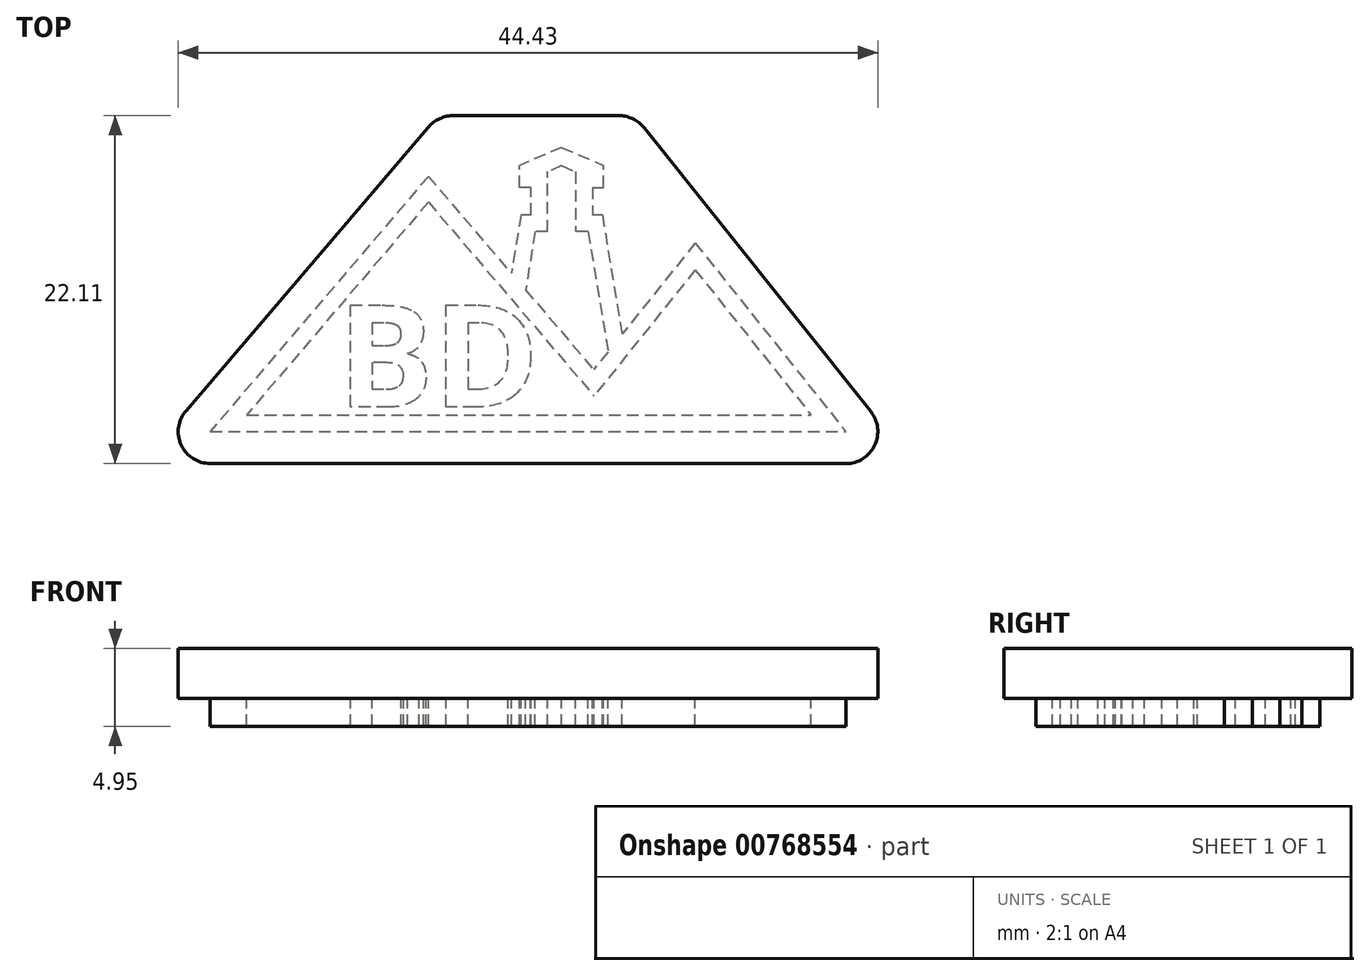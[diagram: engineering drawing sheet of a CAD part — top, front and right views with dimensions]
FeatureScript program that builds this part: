
annotation { "Feature Type Name" : "Feature", "Feature Type Description" : "" }
export const myFeature = defineFeature(function(context is Context, id is Id, definition is map)
    precondition{}
    {
        {
            var Q0;
            Q0=qCreatedBy(makeId("Top.planeOp"),FACE);
            var sketch = newSketch(context, id + "F0", { "sketchPlane" : qUnion([Q0])});
            skPoint(sketch, "E0.middle", {"position": v(0, 0) * mm});
            skLineSegment(sketch, "E1.1", {"start": v(-10.6, 2.98) * mm, "end": v(-5.95, -2.81) * mm});
            skLineSegment(sketch, "E1.2", {"start": v(6.35, 7.21) * mm, "end": v(1.09, 1.05) * mm});
            skLineSegment(sketch, "E2.0", {"start": v(-10.6, 1.27) * mm, "end": v(-17.94, -7.93) * mm});
            skLineSegment(sketch, "E3.0", {"start": v(6.35, 5.57) * mm, "end": v(17.9, -7.93) * mm});
            skLineSegment(sketch, "E3.1", {"start": v(6.35, 5.57) * mm, "end": v(-4.17, -6.74) * mm});
            skLineSegment(sketch, "E3.2", {"start": v(-10.6, 1.27) * mm, "end": v(-4.17, -6.74) * mm});
            skLineSegment(sketch, "E4.0", {"start": v(17.9, -7.93) * mm, "end": v(-17.94, -7.93) * mm});
            skPoint(sketch, "E5", {"position": v(-17.94, -7.93) * mm});
            skPoint(sketch, "E6", {"position": v(17.9, -7.93) * mm});
            skPoint(sketch, "E7", {"position": v(-4.15, -5.07) * mm});
            skPoint(sketch, "E8", {"position": v(-4.17, -6.74) * mm});
            skPoint(sketch, "E9", {"position": v(6.35, 5.57) * mm});
            skPoint(sketch, "E10", {"position": v(-10.6, 1.27) * mm});
            skPoint(sketch, "E11", {"position": v(6.35, 7.21) * mm});
            skPoint(sketch, "E12", {"position": v(-10.6, 2.98) * mm});
            skLineSegment(sketch, "E13.0", {"start": v(-4.7, 4.76) * mm, "end": v(-5.95, -2.81) * mm});
            skLineSegment(sketch, "E13.1", {"start": v(-4.7, 4.76) * mm, "end": v(-4.06, 4.76) * mm});
            skLineSegment(sketch, "E13.2", {"start": v(-0.15, 6.5) * mm, "end": v(0.56, 6.5) * mm});
            skLineSegment(sketch, "E13.3", {"start": v(-0.15, 4.76) * mm, "end": v(-0.15, 6.5) * mm});
            skLineSegment(sketch, "E13.4", {"start": v(-0.15, 4.76) * mm, "end": v(0.48, 4.76) * mm});
            skLineSegment(sketch, "E13.5", {"start": v(0.48, 4.76) * mm, "end": v(1.09, 1.05) * mm});
            skLineSegment(sketch, "E13.6", {"start": v(0.56, 6.5) * mm, "end": v(0.56, 7.9) * mm});
            skLineSegment(sketch, "E13.7", {"start": v(-2.1, 9.05) * mm, "end": v(0.56, 7.9) * mm});
            skLineSegment(sketch, "E13.8", {"start": v(-2.1, 9.05) * mm, "end": v(-4.78, 7.9) * mm});
            skLineSegment(sketch, "E13.9", {"start": v(-4.78, 6.5) * mm, "end": v(-4.78, 7.9) * mm});
            skLineSegment(sketch, "E13.10", {"start": v(-4.06, 6.5) * mm, "end": v(-4.78, 6.5) * mm});
            skLineSegment(sketch, "E13.11", {"start": v(-4.06, 6.5) * mm, "end": v(-4.06, 4.76) * mm});
            skLineSegment(sketch, "E14.0", {"start": v(-3.79, 3.7) * mm, "end": v(-5.06, -3.93) * mm});
            skLineSegment(sketch, "E14.1", {"start": v(-3.79, 3.7) * mm, "end": v(-3, 3.7) * mm});
            skLineSegment(sketch, "E14.2", {"start": v(-3, 7.5) * mm, "end": v(-3, 3.7) * mm});
            skLineSegment(sketch, "E14.3", {"start": v(-2.1, 7.89) * mm, "end": v(-3, 7.5) * mm});
            skLineSegment(sketch, "E14.4", {"start": v(-0.43, 3.7) * mm, "end": v(0.18, 0) * mm});
            skLineSegment(sketch, "E14.5", {"start": v(-1.22, 3.7) * mm, "end": v(-0.43, 3.7) * mm});
            skLineSegment(sketch, "E14.6", {"start": v(-1.22, 3.7) * mm, "end": v(-1.22, 7.5) * mm});
            skLineSegment(sketch, "E14.7", {"start": v(-2.1, 7.89) * mm, "end": v(-1.22, 7.5) * mm});
            skPoint(sketch, "E15", {"position": v(-5.95, -2.81) * mm});
            skPoint(sketch, "E16", {"position": v(-5.06, -3.93) * mm});
            skPoint(sketch, "E17", {"position": v(0.18, 0) * mm});
            skPoint(sketch, "E18", {"position": v(1.09, 1.05) * mm});
            skPoint(sketch, "E19", {"position": v(20.2, -9) * mm});
            skPoint(sketch, "E20", {"position": v(-20.16, -9) * mm});
            skLineSegment(sketch, "E21.trimOffspring", {"start": v(0.18, 0) * mm, "end": v(-4.15, -5.07) * mm});
            skLineSegment(sketch, "E22.trimOffspring", {"start": v(-5.06, -3.93) * mm, "end": v(-4.15, -5.07) * mm});
            skLineSegment(sketch, "E23", {"start": v(20.2, -9) * mm, "end": v(-20.16, -9) * mm});
            skLineSegment(sketch, "E24", {"start": v(6.35, 7.21) * mm, "end": v(20.2, -9) * mm});
            skLineSegment(sketch, "E25", {"start": v(-10.6, 2.98) * mm, "end": v(-20.16, -9) * mm});
            skText(sketch, "E26", { "text": "BD", "fontName": "NotoSans-Bold.ttf"});
            skLineSegment(sketch, "E27", {"start": v(-20.16, -11.03) * mm, "end": v(20.2, -11.03) * mm});
            skArc(sketch, "E28", {"start": v(-21.75, -7.73) * mm, "mid": v(-21.99, -9.88) * mm, "end": v(-20.16, -11.03) * mm});
            skArc(sketch, "E29", {"start": v(20.2, -11.03) * mm, "mid": v(22.05, -9.85) * mm, "end": v(21.75, -7.68) * mm});
            skLineSegment(sketch, "E30", {"start": v(-5.69, 11.08) * mm, "end": v(4.72, 11.08) * mm});
            skArc(sketch, "E31", {"start": v(6.36, 10.32) * mm, "mid": v(5.63, 10.88) * mm, "end": v(4.72, 11.08) * mm});
            skArc(sketch, "E32", {"start": v(-5.69, 11.08) * mm, "mid": v(-6.62, 10.87) * mm, "end": v(-7.37, 10.27) * mm});
            skLineSegment(sketch, "E33.trimOffspring", {"start": v(-7.37, 10.27) * mm, "end": v(-21.75, -7.73) * mm});
            skLineSegment(sketch, "E34.trimOffspring", {"start": v(6.36, 10.32) * mm, "end": v(21.75, -7.68) * mm});
            skPoint(sketch, "E35.start.orphan", {"position": v(0, 19.5) * mm});
            skLineSegment(sketch, "E36", {"start": v(24.3, 18.38) * mm, "end": v(24.3, -20.56) * mm});
            skLineSegment(sketch, "E37.MirrorCS", {"start": v(52.66, 6.5) * mm, "end": v(53.37, 6.5) * mm});
            skLineSegment(sketch, "E38.MirrorCS", {"start": v(50.7, 7.89) * mm, "end": v(51.6, 7.5) * mm});
            skLineSegment(sketch, "E39.MirrorCS", {"start": v(50.7, 7.89) * mm, "end": v(49.82, 7.5) * mm});
            skLineSegment(sketch, "E40.MirrorCS", {"start": v(48.75, 4.76) * mm, "end": v(48.12, 4.76) * mm});
            skLineSegment(sketch, "E41.MirrorCS", {"start": v(49.03, 3.7) * mm, "end": v(48.42, 0) * mm});
            skLineSegment(sketch, "E42.MirrorCS", {"start": v(52.66, 6.5) * mm, "end": v(52.66, 4.76) * mm});
            skLineSegment(sketch, "E43.MirrorCS", {"start": v(53.65, -3.93) * mm, "end": v(52.75, -5.07) * mm});
            skLineSegment(sketch, "E44.MirrorCS", {"start": v(49.82, 3.7) * mm, "end": v(49.03, 3.7) * mm});
            skLineSegment(sketch, "E45.MirrorCS", {"start": v(53.37, 6.5) * mm, "end": v(53.37, 7.9) * mm});
            skLineSegment(sketch, "E46.MirrorCS", {"start": v(49.82, 3.7) * mm, "end": v(49.82, 7.5) * mm});
            skLineSegment(sketch, "E47.MirrorCS", {"start": v(48.12, 4.76) * mm, "end": v(47.51, 1.05) * mm});
            skLineSegment(sketch, "E48.MirrorCS", {"start": v(48.75, 4.76) * mm, "end": v(48.75, 6.5) * mm});
            skLineSegment(sketch, "E49.MirrorCS", {"start": v(48.75, 6.5) * mm, "end": v(48.04, 6.5) * mm});
            skLineSegment(sketch, "E50.MirrorCS", {"start": v(53.3, 4.76) * mm, "end": v(52.66, 4.76) * mm});
            skLineSegment(sketch, "E51.MirrorCS", {"start": v(52.39, 3.7) * mm, "end": v(51.6, 3.7) * mm});
            skLineSegment(sketch, "E52.MirrorCS", {"start": v(51.6, 7.5) * mm, "end": v(51.6, 3.7) * mm});
            skArc(sketch, "E53.MirrorCS", {"start": v(54.28, 11.08) * mm, "mid": v(55.22, 10.87) * mm, "end": v(55.97, 10.27) * mm});
            skLineSegment(sketch, "E54.MirrorCS", {"start": v(50.7, 9.05) * mm, "end": v(48.04, 7.9) * mm});
            skLineSegment(sketch, "E55.MirrorCS", {"start": v(48.04, 6.5) * mm, "end": v(48.04, 7.9) * mm});
            skLineSegment(sketch, "E56.MirrorCS", {"start": v(50.7, 9.05) * mm, "end": v(53.37, 7.9) * mm});
            skArc(sketch, "E57.MirrorCS", {"start": v(42.23, 10.32) * mm, "mid": v(42.97, 10.88) * mm, "end": v(43.87, 11.08) * mm});
            skLineSegment(sketch, "E58.MirrorCS", {"start": v(59.19, 1.27) * mm, "end": v(66.54, -7.93) * mm});
            skArc(sketch, "E59.MirrorCS", {"start": v(70.34, -7.73) * mm, "mid": v(70.59, -9.88) * mm, "end": v(68.76, -11.03) * mm});
            skPoint(sketch, "E60.MirrorP", {"position": v(48.6, 0) * mm});
            skArc(sketch, "E61.MirrorCS", {"start": v(28.4, -11.03) * mm, "mid": v(26.55, -9.85) * mm, "end": v(26.85, -7.68) * mm});
            skLineSegment(sketch, "E62.MirrorCS", {"start": v(42.25, 7.21) * mm, "end": v(28.4, -9) * mm});
            skLineSegment(sketch, "E63.MirrorCS", {"start": v(48.42, 0) * mm, "end": v(52.75, -5.07) * mm});
            skLineSegment(sketch, "E64.MirrorCS", {"start": v(30.7, -7.93) * mm, "end": v(66.54, -7.93) * mm});
            skPoint(sketch, "E65.MirrorP", {"position": v(52.77, -6.74) * mm});
            skPoint(sketch, "E66.MirrorP", {"position": v(59.19, 1.27) * mm});
            skPoint(sketch, "E67.MirrorP", {"position": v(42.25, 5.57) * mm});
            skPoint(sketch, "E68.MirrorP", {"position": v(52.75, -5.07) * mm});
            skPoint(sketch, "E69.MirrorP", {"position": v(48.42, 0) * mm});
            skLineSegment(sketch, "E70.MirrorCS", {"start": v(54.28, 11.08) * mm, "end": v(43.87, 11.08) * mm});
            skLineSegment(sketch, "E71.MirrorCS", {"start": v(42.25, 5.57) * mm, "end": v(52.77, -6.74) * mm});
            skLineSegment(sketch, "E72.MirrorCS", {"start": v(59.19, 1.27) * mm, "end": v(52.77, -6.74) * mm});
            skLineSegment(sketch, "E73.MirrorCS", {"start": v(42.25, 7.21) * mm, "end": v(47.51, 1.05) * mm});
            skLineSegment(sketch, "E74.MirrorCS", {"start": v(68.76, -11.03) * mm, "end": v(28.4, -11.03) * mm});
            skPoint(sketch, "E75.MirrorP", {"position": v(30.7, -7.93) * mm});
            skLineSegment(sketch, "E76.MirrorCS", {"start": v(42.25, 5.57) * mm, "end": v(30.7, -7.93) * mm});
            skLineSegment(sketch, "E77.MirrorCS", {"start": v(55.97, 10.27) * mm, "end": v(70.34, -7.73) * mm});
            skLineSegment(sketch, "E78.MirrorCS", {"start": v(53.3, 4.76) * mm, "end": v(54.55, -2.81) * mm});
            skLineSegment(sketch, "E79.MirrorCS", {"start": v(28.4, -9) * mm, "end": v(68.76, -9) * mm});
            skLineSegment(sketch, "E80.MirrorCS", {"start": v(52.39, 3.7) * mm, "end": v(53.65, -3.93) * mm});
            skLineSegment(sketch, "E81.MirrorCS", {"start": v(59.2, 2.98) * mm, "end": v(68.76, -9) * mm});
            skPoint(sketch, "E82.MirrorP", {"position": v(47.51, 1.05) * mm});
            skLineSegment(sketch, "E83.MirrorCS", {"start": v(59.2, 2.98) * mm, "end": v(54.55, -2.81) * mm});
            skPoint(sketch, "E84.MirrorP", {"position": v(59.2, 2.98) * mm});
            skPoint(sketch, "E85.MirrorP", {"position": v(66.54, -7.93) * mm});
            skPoint(sketch, "E86.MirrorP", {"position": v(53.65, -3.93) * mm});
            skLineSegment(sketch, "E87.MirrorCS", {"start": v(42.23, 10.32) * mm, "end": v(26.85, -7.68) * mm});
            skPoint(sketch, "E88.MirrorP", {"position": v(42.25, 7.21) * mm});
            skPoint(sketch, "E89.MirrorP", {"position": v(54.55, -2.81) * mm});
            skText(sketch, "E90", { "text": "BD", "fontName": "OpenSans-Bold.ttf"});
            skPoint(sketch, "E90.secondSnap0", {"position": v(36.48, -1.18) * mm});
            const initialGuessF0  = {"E26": [0.0005, -0.00744, 1, 0, 0.00652], "E90": [0.03648, -0.00744, 1, 0, 0.00652]};
            skSetInitialGuess(sketch, initialGuessF0);
            skSolve(sketch);
        }
        {
            var Q0;
            Q0=makeQuery(id+"F0.imprint","IMPRINT",FACE,{"disambiguationData":[TD([[makeQuery(id+"F0.imprint","IMPRINT",EDGE,{"derivedFrom":sQuery(id+"F0.wireOp",EDGE,"E37.MirrorCS")}),-1.0]])]});
            var Q1;
            Q1=makeQuery(id+"F0.imprint","IMPRINT",FACE,{"disambiguationData":[TD([[makeQuery(id+"F0.imprint","IMPRINT",EDGE,{"derivedFrom":sQuery(id+"F0.wireOp",EDGE,"E90.sketch_text.stroke-32")}),1.0]])]});
            var Q2;
            Q2=makeQuery(id+"F0.imprint","IMPRINT",FACE,{"disambiguationData":[TD([[makeQuery(id+"F0.imprint","IMPRINT",EDGE,{"derivedFrom":sQuery(id+"F0.wireOp",EDGE,"E37.MirrorCS")}),1.0]])]});
            var Q3;
            Q3=makeQuery(id+"F0.imprint","IMPRINT",FACE,{"disambiguationData":[TD([[makeQuery(id+"F0.imprint","IMPRINT",EDGE,{"derivedFrom":sQuery(id+"F0.wireOp",EDGE,"E90.sketch_text.stroke-0")}),-1.0]])]});
            var Q4;
            Q4=makeQuery(id+"F0.imprint","IMPRINT",FACE,{"disambiguationData":[TD([[makeQuery(id+"F0.imprint","IMPRINT",EDGE,{"derivedFrom":sQuery(id+"F0.wireOp",EDGE,"E38.MirrorCS")}),-1.0]])]});
            var Q5;
            Q5=makeQuery(id+"F0.imprint","IMPRINT",FACE,{"disambiguationData":[TD([[makeQuery(id+"F0.imprint","IMPRINT",EDGE,{"derivedFrom":sQuery(id+"F0.wireOp",EDGE,"E64.MirrorCS")}),1.0]])]});
            var Q6;
            Q6=makeQuery(id+"F0.imprint","IMPRINT",FACE,{"disambiguationData":[TD([[makeQuery(id+"F0.imprint","IMPRINT",EDGE,{"derivedFrom":sQuery(id+"F0.wireOp",EDGE,"E90.sketch_text.stroke-25")}),-1.0]])]});
            var Q7;
            Q7=makeQuery(id+"F0.imprint","IMPRINT",FACE,{"disambiguationData":[TD([[makeQuery(id+"F0.imprint","IMPRINT",EDGE,{"derivedFrom":sQuery(id+"F0.wireOp",EDGE,"E90.sketch_text.stroke-12")}),1.0]])]});
            var Q8;
            Q8=makeQuery(id+"F0.imprint","IMPRINT",FACE,{"disambiguationData":[TD([[makeQuery(id+"F0.imprint","IMPRINT",EDGE,{"derivedFrom":sQuery(id+"F0.wireOp",EDGE,"E90.sketch_text.stroke-19")}),1.0]])]});
            extrude(context, id + "F1", {"entities" : qUnion([Q0, Q1, Q2, Q3, Q4, Q5, Q6, Q7, Q8]), "depth" : 3.17 * mm, "offsetDistance" : 25.4 * mm});
        }
        {
            var Q0;
            Q0=makeQuery(id+"F0.imprint","IMPRINT",FACE,{"disambiguationData":[TD([[makeQuery(id+"F0.imprint","IMPRINT",EDGE,{"derivedFrom":sQuery(id+"F0.wireOp",EDGE,"E37.MirrorCS")}),1.0]])]});
            var Q1;
            Q1=makeQuery(id+"F0.imprint","IMPRINT",FACE,{"disambiguationData":[TD([[makeQuery(id+"F0.imprint","IMPRINT",EDGE,{"derivedFrom":sQuery(id+"F0.wireOp",EDGE,"E90.sketch_text.stroke-0")}),-1.0]])]});
            var Q2;
            Q2=makeQuery(id+"F0.imprint","IMPRINT",FACE,{"disambiguationData":[TD([[makeQuery(id+"F0.imprint","IMPRINT",EDGE,{"derivedFrom":sQuery(id+"F0.wireOp",EDGE,"E90.sketch_text.stroke-25")}),-1.0]])]});
            extrude(context, id + "F2", {"entities" : qUnion([Q0, Q1, Q2]), "operationType" : NewBodyOperationType.ADD, "oppositeDirection" : true, "depth" : 1.78 * mm, "offsetDistance" : 25.4 * mm});
        }
    });
